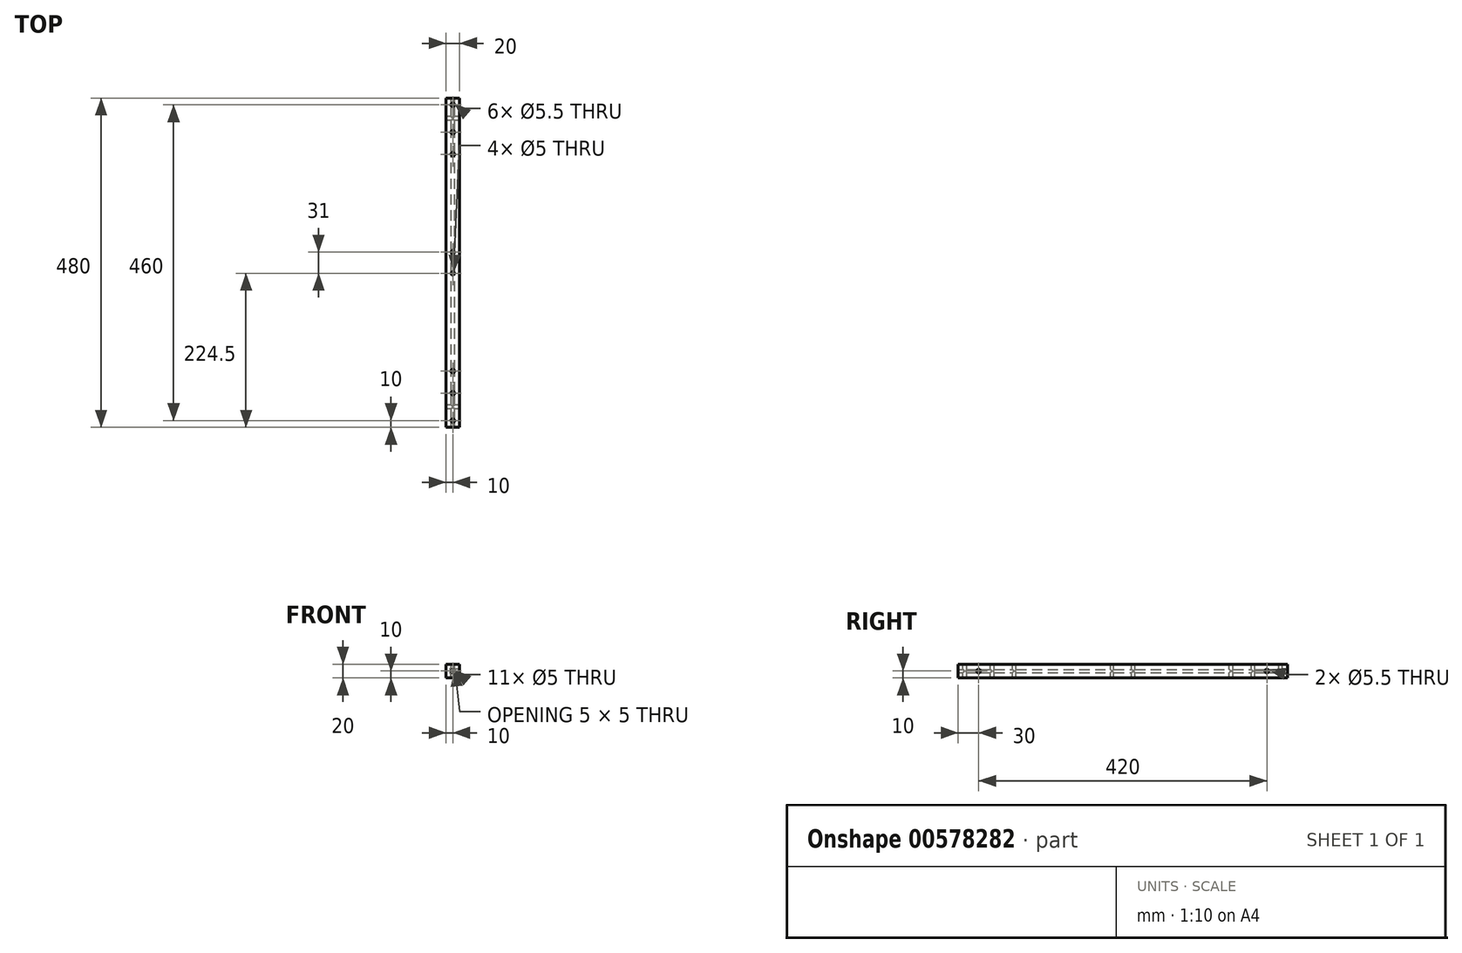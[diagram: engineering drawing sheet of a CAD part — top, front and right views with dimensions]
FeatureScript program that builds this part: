
annotation { "Feature Type Name" : "Feature", "Feature Type Description" : "" }
export const myFeature = defineFeature(function(context is Context, id is Id, definition is map)
    precondition{}
    {
        {
            var Q0;
            Q0=qCreatedBy(makeId("Front.planeOp"),FACE);
            var sketch = newSketch(context, id + "F0", { "sketchPlane" : qUnion([Q0])});
            skLineSegment(sketch, "E0.bottom", {"start": v(-10, 10) * mm, "end": v(10, 10) * mm});
            skLineSegment(sketch, "E0.top", {"start": v(-10, -10) * mm, "end": v(10, -10) * mm});
            skLineSegment(sketch, "E0.left", {"start": v(-10, 10) * mm, "end": v(-10, -10) * mm});
            skLineSegment(sketch, "E0.right", {"start": v(10, 10) * mm, "end": v(10, -10) * mm});
            skPoint(sketch, "E0.middle", {"position": v(0, 0) * mm});
            skCircle(sketch, "E1", {"center": v(0, 0) * mm, "radius": 2.5 * mm});
            skSolve(sketch);
        }
        {
            var Q0;
            Q0=qSketchRegion(id+"F0",true);
            extrude(context, id + "F1", {"entities" : qUnion([Q0]), "endBound" : BoundingType.SYMMETRIC, "depth" : 480 * mm, "offsetDistance" : 25 * mm});
        }
        {
            var Q0;
            Q0=makeQuery(id+"F1.opExtrude","SWEPT_FACE",FACE,{"disambiguationData":[OSD([sQuery(id+"F0.wireOp",EDGE,"E0.left")])]});
            var sketch = newSketch(context, id + "F2", { "sketchPlane" : qUnion([Q0])});
            skCircle(sketch, "E2", {"center": v(-210, 0) * mm, "radius": 2.75 * mm});
            skPoint(sketch, "E2.centerSnap0", {"position": v(-240, 0) * mm});
            skCircle(sketch, "E3", {"center": v(210, 0) * mm, "radius": 2.75 * mm});
            skSolve(sketch);
        }
        {
            var Q0;
            Q0=qSketchRegion(id+"F2",true);
            extrude(context, id + "F3", {"entities" : qUnion([Q0]), "operationType" : NewBodyOperationType.REMOVE, "oppositeDirection" : true, "depth" : 20 * mm, "offsetDistance" : 25 * mm});
        }
        {
            var Q0;
            Q0=qCreatedBy(makeId("Top.planeOp"),FACE);
            var sketch = newSketch(context, id + "F4", { "sketchPlane" : qUnion([Q0])});
            skCircle(sketch, "E4", {"center": v(0, 15.5) * mm, "radius": 2.5 * mm});
            skCircle(sketch, "E5.MirrorC", {"center": v(0, -15.5) * mm, "radius": 2.5 * mm});
            skCircle(sketch, "E6", {"center": v(0, -158) * mm, "radius": 2.75 * mm});
            skCircle(sketch, "E7", {"center": v(0, -190) * mm, "radius": 2.75 * mm});
            skCircle(sketch, "E8", {"center": v(0, 158) * mm, "radius": 2.75 * mm});
            skCircle(sketch, "E9", {"center": v(0, 190) * mm, "radius": 2.75 * mm});
            skCircle(sketch, "E10", {"center": v(0, -230) * mm, "radius": 2.75 * mm});
            skCircle(sketch, "E11", {"center": v(0, 230) * mm, "radius": 2.75 * mm});
            skSolve(sketch);
        }
        {
            var Q0;
            Q0=qSketchRegion(id+"F4",true);
            extrude(context, id + "F5", {"entities" : qUnion([Q0]), "operationType" : NewBodyOperationType.REMOVE, "endBound" : BoundingType.SYMMETRIC, "oppositeDirection" : true, "depth" : 20 * mm, "offsetDistance" : 25 * mm});
        }
    });
